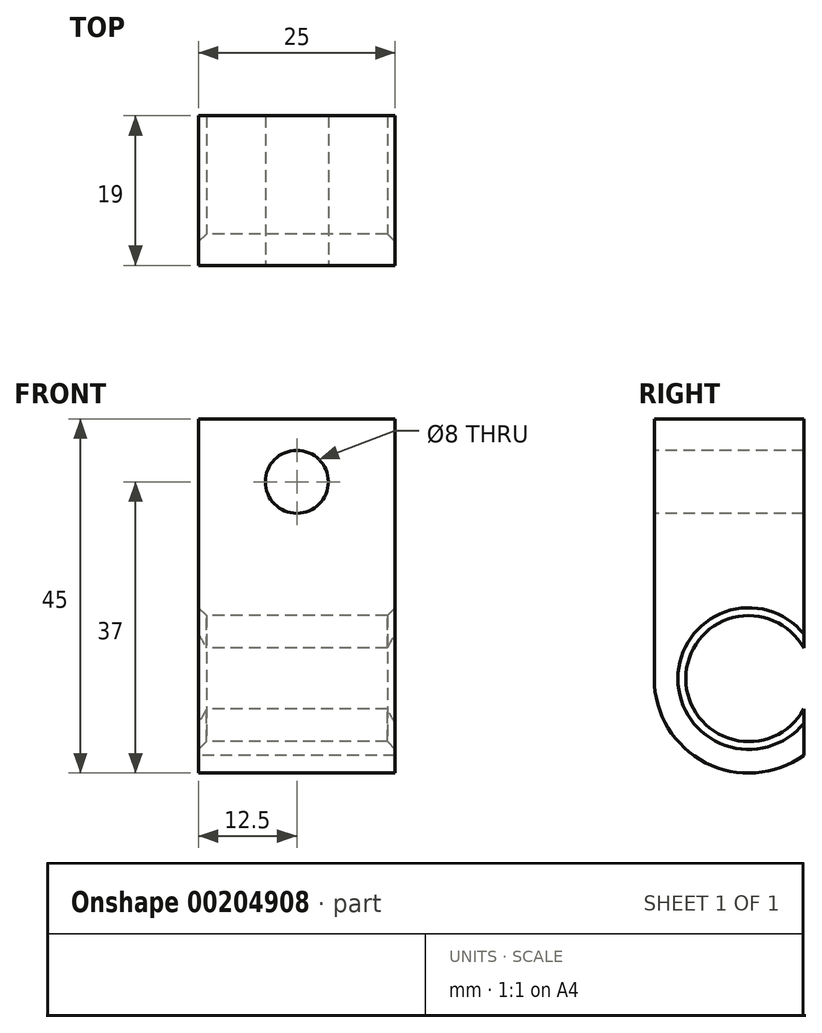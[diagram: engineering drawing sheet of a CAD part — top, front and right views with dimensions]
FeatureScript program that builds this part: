
annotation { "Feature Type Name" : "Feature", "Feature Type Description" : "" }
export const myFeature = defineFeature(function(context is Context, id is Id, definition is map)
    precondition{}
    {
        {
            var Q0;
            Q0=qCreatedBy(makeId("Right.planeOp"),FACE);
            var sketch = newSketch(context, id + "F0", { "sketchPlane" : qUnion([Q0])});
            skCircle(sketch, "E0", {"center": v(0, 0) * mm, "radius": 8 * mm});
            skCircle(sketch, "E1", {"center": v(0, 0) * mm, "radius": 12 * mm});
            skLineSegment(sketch, "E2", {"start": v(0, 0) * mm, "end": v(12, 0) * mm});
            skLineSegment(sketch, "E3", {"start": v(0, 0) * mm, "end": v(-12, 0) * mm});
            skLineSegment(sketch, "E4", {"start": v(0, 0) * mm, "end": v(0, 25) * mm});
            skLineSegment(sketch, "E5", {"start": v(0, 25) * mm, "end": v(0, 29) * mm});
            skLineSegment(sketch, "E6", {"start": v(0, 29) * mm, "end": v(0, 33) * mm});
            skLineSegment(sketch, "E7", {"start": v(12, 0) * mm, "end": v(12, 33) * mm});
            skLineSegment(sketch, "E8", {"start": v(12, 33) * mm, "end": v(0, 33) * mm});
            skLineSegment(sketch, "E9", {"start": v(-12, 0) * mm, "end": v(-12, 33) * mm});
            skLineSegment(sketch, "E10", {"start": v(-12, 33) * mm, "end": v(0, 33) * mm});
            skSolve(sketch);
        }
        {
            var Q0;
            {var subQ0=sQuery(id+"F0.wireOp",EDGE,"E4");var subQ1=sQuery(id+"F0.wireOp",EDGE,"E0");var subQ2=makeQuery(id+"F0.imprint","INTERSECT",VERTEX,{"derivedFrom":[subQ1,subQ0]});Q0=makeQuery(id+"F0.imprint","IMPRINT",FACE,{"disambiguationData":[TD([[makeQuery(id+"F0.imprint","IMPRINT",EDGE,{"disambiguationData":[TD([[subQ2,1.0]])],"derivedFrom":subQ1}),-1.0]])]});}
            var Q1;
            {var subQ0=sQuery(id+"F0.wireOp",EDGE,"E2");var subQ1=sQuery(id+"F0.wireOp",EDGE,"E0");var subQ2=makeQuery(id+"F0.imprint","INTERSECT",VERTEX,{"derivedFrom":[subQ1,subQ0]});Q1=makeQuery(id+"F0.imprint","IMPRINT",FACE,{"disambiguationData":[TD([[makeQuery(id+"F0.imprint","IMPRINT",EDGE,{"disambiguationData":[TD([[subQ2,1.0]])],"derivedFrom":subQ1}),-1.0]])]});}
            var Q2;
            {var subQ0=sQuery(id+"F0.wireOp",EDGE,"E4");var subQ1=sQuery(id+"F0.wireOp",EDGE,"E0");var subQ2=makeQuery(id+"F0.imprint","INTERSECT",VERTEX,{"derivedFrom":[subQ1,subQ0]});Q2=makeQuery(id+"F0.imprint","IMPRINT",FACE,{"disambiguationData":[TD([[makeQuery(id+"F0.imprint","IMPRINT",EDGE,{"disambiguationData":[TD([[subQ2,-1.0]])],"derivedFrom":subQ1}),-1.0]])]});}
            var Q3;
            {var subQ0=sQuery(id+"F0.wireOp",EDGE,"E5");Q3=makeQuery(id+"F0.imprint","IMPRINT",FACE,{"disambiguationData":[TD([[makeQuery(id+"F0.imprint","IMPRINT",EDGE,{"derivedFrom":subQ0}),1.0]])]});}
            var Q4;
            {var subQ0=sQuery(id+"F0.wireOp",EDGE,"E5");Q4=makeQuery(id+"F0.imprint","IMPRINT",FACE,{"disambiguationData":[TD([[makeQuery(id+"F0.imprint","IMPRINT",EDGE,{"derivedFrom":subQ0}),-1.0]])]});}
            extrude(context, id + "F1", {"entities" : qUnion([Q0, Q1, Q2, Q3, Q4]), "depth" : 25 * mm});
        }
        {
            var Q0;
            Q0=makeQuery(id+"F1.opExtrude","CAP_EDGE",EDGE,{"disambiguationData":[OSD([sQuery(id+"F0.wireOp",EDGE,"E0")])],"isStart":false});
            var Q1;
            Q1=makeQuery(id+"F1.opExtrude","CAP_EDGE",EDGE,{"disambiguationData":[OSD([sQuery(id+"F0.wireOp",EDGE,"E0")])],"isStart":true});
            chamfer(context, id + "F2", {"entities" : qUnion([Q0, Q1]), "width" : 1 * mm, "tangentPropagation" : true});
        }
        {
            var Q0;
            Q0=makeQuery(id+"F1.opExtrude","SWEPT_FACE",FACE,{"disambiguationData":[OSD([sQuery(id+"F0.wireOp",EDGE,"E7")])]});
            var sketch = newSketch(context, id + "F3", { "sketchPlane" : qUnion([Q0])});
            skLineSegment(sketch, "E11.bottom", {"start": v(-25, 33) * mm, "end": v(0, 33) * mm});
            skLineSegment(sketch, "E11.top", {"start": v(-25, -17) * mm, "end": v(0, -17) * mm});
            skLineSegment(sketch, "E11.left", {"start": v(-25, 33) * mm, "end": v(-25, -17) * mm});
            skLineSegment(sketch, "E11.right", {"start": v(0, 33) * mm, "end": v(0, -17) * mm});
            skSolve(sketch);
        }
        {
            var Q0;
            {var subQ0=sQuery(id+"F3.wireOp",EDGE,"E11.bottom");Q0=makeQuery(id+"F3.imprint","IMPRINT",FACE,{"disambiguationData":[TD([[makeQuery(id+"F3.imprint","IMPRINT",EDGE,{"derivedFrom":subQ0}),-1.0]])]});}
            var Q1;
            {var subQ0=sQuery(id+"F3.wireOp",EDGE,"E11.top");Q1=makeQuery(id+"F3.imprint","IMPRINT",FACE,{"disambiguationData":[TD([[makeQuery(id+"F3.imprint","IMPRINT",EDGE,{"derivedFrom":subQ0}),1.0]])]});}
            extrude(context, id + "F4", {"entities" : qUnion([Q0, Q1]), "operationType" : NewBodyOperationType.REMOVE, "oppositeDirection" : true, "depth" : 5 * mm});
        }
        {
            var Q0;
            Q0=makeQuery(id+"F1.opExtrude","SWEPT_FACE",FACE,{"disambiguationData":[OSD([sQuery(id+"F0.wireOp",EDGE,"E9")])]});
            var sketch = newSketch(context, id + "F5", { "sketchPlane" : qUnion([Q0])});
            skLineSegment(sketch, "E12", {"start": v(0, 25) * mm, "end": v(12.5, 25) * mm});
            skLineSegment(sketch, "E13", {"start": v(12.5, 25) * mm, "end": v(25, 25) * mm});
            skCircle(sketch, "E14", {"center": v(12.5, 25) * mm, "radius": 4 * mm});
            skSolve(sketch);
        }
        {
            var Q0;
            {var subQ0=sQuery(id+"F5.wireOp",EDGE,"E13");var subQ1=sQuery(id+"F5.wireOp",EDGE,"E12");var subQ2=makeQuery(id+"F5.imprint","INTERSECT",VERTEX,{"derivedFrom":[subQ1,subQ0]});Q0=makeQuery(id+"F5.imprint","IMPRINT",FACE,{"disambiguationData":[TD([[makeQuery(id+"F5.imprint","IMPRINT",EDGE,{"disambiguationData":[TD([[subQ2,1.0]])],"derivedFrom":subQ1}),-1.0]])]});}
            var Q1;
            {var subQ0=sQuery(id+"F5.wireOp",EDGE,"E13");var subQ1=sQuery(id+"F5.wireOp",EDGE,"E12");var subQ2=makeQuery(id+"F5.imprint","INTERSECT",VERTEX,{"derivedFrom":[subQ1,subQ0]});Q1=makeQuery(id+"F5.imprint","IMPRINT",FACE,{"disambiguationData":[TD([[makeQuery(id+"F5.imprint","IMPRINT",EDGE,{"disambiguationData":[TD([[subQ2,1.0]])],"derivedFrom":subQ1}),1.0]])]});}
            extrude(context, id + "F6", {"entities" : qUnion([Q0, Q1]), "operationType" : NewBodyOperationType.REMOVE, "oppositeDirection" : true, "depth" : 25 * mm});
        }
    });
